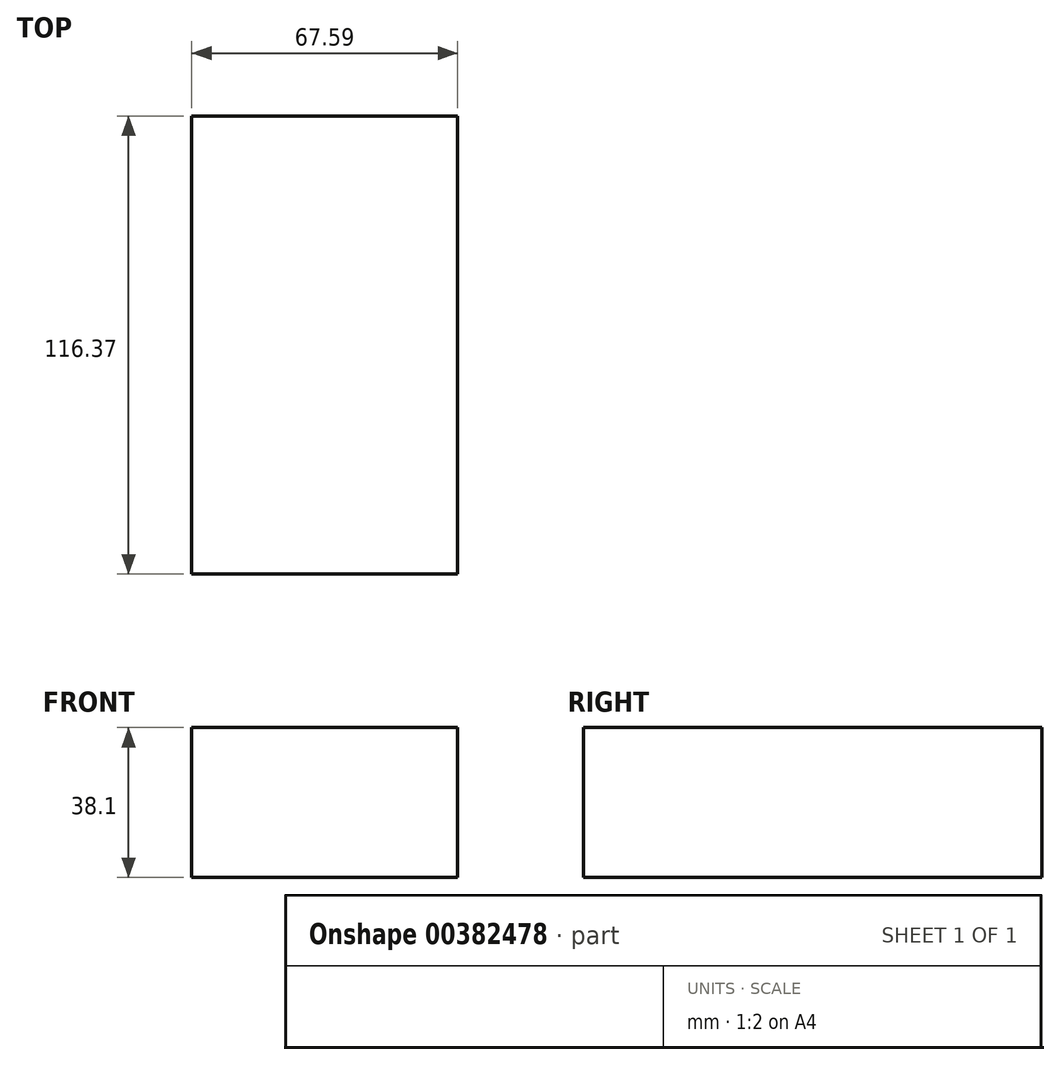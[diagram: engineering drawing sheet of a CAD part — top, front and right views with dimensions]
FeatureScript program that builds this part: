
annotation { "Feature Type Name" : "Feature", "Feature Type Description" : "" }
export const myFeature = defineFeature(function(context is Context, id is Id, definition is map)
    precondition{}
    {
        {
            var Q0;
            Q0=qCreatedBy(makeId("Top.planeOp"),FACE);
            var sketch = newSketch(context, id + "F0", { "sketchPlane" : qUnion([Q0])});
            skLineSegment(sketch, "E0.bottom", {"start": v(35.4, -59.99) * mm, "end": v(-32.2, -59.99) * mm});
            skLineSegment(sketch, "E0.top", {"start": v(35.4, 56.38) * mm, "end": v(-32.2, 56.38) * mm});
            skLineSegment(sketch, "E0.left", {"start": v(35.4, -59.99) * mm, "end": v(35.4, 56.38) * mm});
            skLineSegment(sketch, "E0.right", {"start": v(-32.2, -59.99) * mm, "end": v(-32.2, 56.38) * mm});
            skSolve(sketch);
        }
        {
            var Q0;
            Q0 = qSketchRegion(id + "F0", true);
            extrude(context, id + "F1", {"entities" : qUnion([Q0]), "oppositeDirection" : true, "depth" : 38.1 * mm});
        }
    });
